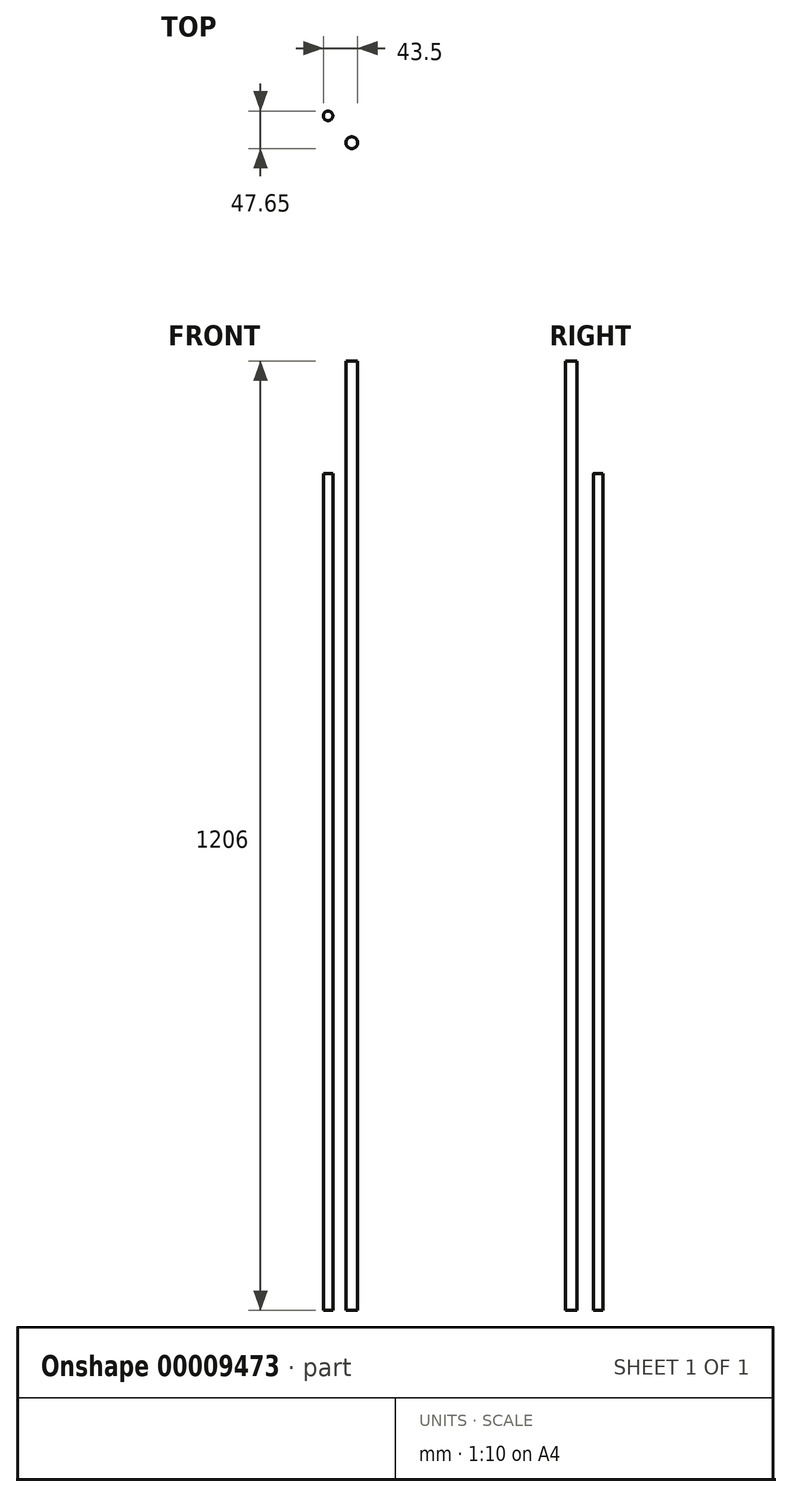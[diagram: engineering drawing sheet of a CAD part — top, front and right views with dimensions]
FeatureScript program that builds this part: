
annotation { "Feature Type Name" : "Feature", "Feature Type Description" : "" }
export const myFeature = defineFeature(function(context is Context, id is Id, definition is map)
    precondition{}
    {
        {
            var Q0;
            Q0=qCreatedBy(makeId("Top.planeOp"),FACE);
            var sketch = newSketch(context, id + "F0", { "sketchPlane" : qUnion([Q0])});
            skCircle(sketch, "E0", {"center": v(-3.12, 0) * mm, "radius": 6 * mm});
            skSolve(sketch);
        }
        {
            var Q0;
            Q0 = qSketchRegion(id + "F0", true);
            extrude(context, id + "F1", {"entities" : qUnion([Q0]), "depth" : 1063 * mm});
        }
        {
            var Q0;
            Q0=qCreatedBy(makeId("Top.planeOp"),FACE);
            var sketch = newSketch(context, id + "F2", { "sketchPlane" : qUnion([Q0])});
            skCircle(sketch, "E1", {"center": v(26.88, -34.15) * mm, "radius": 7.5 * mm});
            skSolve(sketch);
        }
        {
            var Q0;
            Q0 = qSketchRegion(id + "F2", true);
            extrude(context, id + "F3", {"entities" : qUnion([Q0]), "depth" : 1206 * mm});
        }
    });
